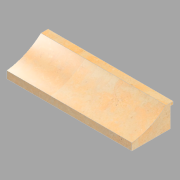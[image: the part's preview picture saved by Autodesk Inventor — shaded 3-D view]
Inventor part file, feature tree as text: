
AUTODESK INVENTOR PART (.ipt)
format: ipt  version: 2022.2 (Build 262287010, 287A)  size: 139,264 bytes
history: native  units: in
note: dims shown in document units (in); Inventor stores cm internally (conversion verified against a paired STEP export)
features: revolve x2, other x1, direct_edit x1
ambient origin geometry x8: Origin, YZ Plane, XZ Plane, XY Plane, X Axis, Y Axis, Z Axis, Center Point
bodies: Solid1 (feature_tree)
feature tree (4):
  other  "North (9)"
  direct_edit  "Direct Edit1"
  revolve  "Rotate1"  [1 undecoded]
  revolve  "Rotate2"  Angle=90.0deg
note: 1 required parameter value undecoded (feature->parameter linkage not recoverable at this tier; creation-order binding heuristic only, values carry confidence <= 0.55)
